# Revit family: Lighting-Troffer-Cooper-Corelite-Bridge-22BRG-24BRG-LD2
name_source: partatom
category: Lighting Fixtures
revit_build: Autodesk Revit 2014 (Build: 20130308_1515(x64)
units: mm (PartAtom-declared; Revit-internal decimal feet)

## types (1)
- Lighting-Troffer-Cooper-Corelite-Bridge-22BRG-24BRG-LD2
    120 Volts = Yes
    277 Volts = No
    Apparent Load = 0 VA
    Assembly Code = D5020200
    Color Filter = 16777215
    Connector Description = Power In
    Default Elevation = 0' - 0"
    Description = Bridge - Recessed LED
    Dimming Lamp Color Temperature Shift = <None>
    Emit Shape Visible in Rendering = No
    Emit from Rectangle Length = 1' - 10 3/8"
    Emit from Rectangle Width = 0' - 0 3/16"
    Fixture Height = 0' - 3 7/8"
    Fixture Length = 1' - 11 3/8"
    Fixture Width = 1' - 11 5/8"
    LED Length = 1' - 10 3/8"
    Lamp = LED
    Load Classification = Lighting
    Manufacturer = Cooper Lighting
    Model = 22BRG and 24BRG
    Photometric Web File = Select File
    Power Factor = 1
    Product Page URL = http://www.cooperindustries.com
    Square Pattern Array = 7
    Square Pattern Optic = Yes
    Tilt Angle = 90.00°
    Type Comments = 2 x 2 and 2 x 4
    URL = www.eaton.com/lighting
    Voltage = 120 V

## geometry (parser evidence)
native form markers: Blend x2, Sweep x1
no freeform markers — native parametric forms only
